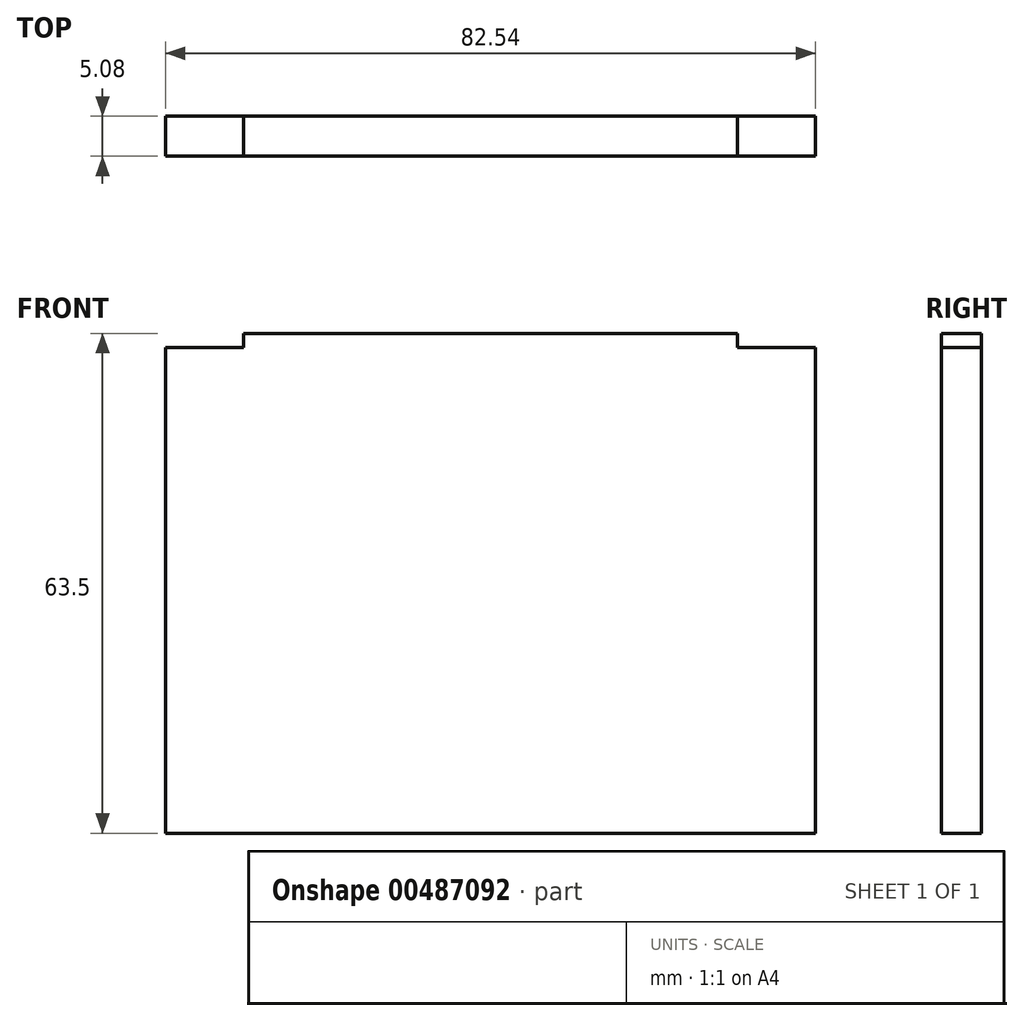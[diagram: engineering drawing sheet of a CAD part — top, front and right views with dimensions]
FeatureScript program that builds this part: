
annotation { "Feature Type Name" : "Feature", "Feature Type Description" : "" }
export const myFeature = defineFeature(function(context is Context, id is Id, definition is map)
    precondition{}
    {
        {
            var Q0;
            Q0=qCreatedBy(makeId("Front.planeOp"),FACE);
            var sketch = newSketch(context, id + "F0", { "sketchPlane" : qUnion([Q0])});
            skLineSegment(sketch, "E0.bottom", {"start": v(-31.37, 34.8) * mm, "end": v(31.37, 34.8) * mm});
            skLineSegment(sketch, "E0.top", {"start": v(-41.27, -28.7) * mm, "end": v(41.28, -28.7) * mm});
            skLineSegment(sketch, "E0.left", {"start": v(-41.27, 33.01) * mm, "end": v(-41.27, -28.7) * mm});
            skLineSegment(sketch, "E0.right", {"start": v(41.28, 33.01) * mm, "end": v(41.28, -28.7) * mm});
            skLineSegment(sketch, "E1.top", {"start": v(41.28, 33.01) * mm, "end": v(31.37, 33.01) * mm});
            skLineSegment(sketch, "E1.right", {"start": v(31.37, 34.8) * mm, "end": v(31.37, 33.01) * mm});
            skLineSegment(sketch, "E2.MirrorCS", {"start": v(-41.28, 33.01) * mm, "end": v(-31.37, 33.01) * mm});
            skLineSegment(sketch, "E3.MirrorCS", {"start": v(-31.37, 34.8) * mm, "end": v(-31.37, 33.01) * mm});
            skPoint(sketch, "E4.orphan", {"position": v(41.28, 34.8) * mm});
            skPoint(sketch, "E5.MirrorCS.end.orphan", {"position": v(-41.28, 33.01) * mm});
            skPoint(sketch, "E5.MirrorCS.start.orphan", {"position": v(-41.28, 34.8) * mm});
            skSolve(sketch);
        }
        {
            var Q0;
            Q0 = qSketchRegion(id + "F0", true);
            extrude(context, id + "F1", {"entities" : qUnion([Q0]), "depth" : 5.08 * mm});
        }
    });
